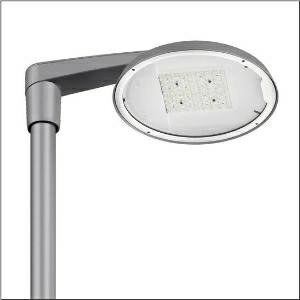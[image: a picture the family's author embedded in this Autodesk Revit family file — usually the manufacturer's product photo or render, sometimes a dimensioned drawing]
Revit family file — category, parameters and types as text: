
# Revit family: dl_50_iq_mini___st0_5a_5xa248b31f08le_1359
name_source: partatom
category: Lighting Fixtures
units: mm (PartAtom-declared; Revit-internal decimal feet)

## family parameters
Cut with Voids When Loaded = No
Host = Face
Light Source = No
Part Type = Normal
Room Calculation Point = No
Round Connector Dimension = Use Diameter
Shared = No

## types (1)
- --- (1 x LED, 10390 lm, 67.4 W, 3000K)
    Apparent Load = 67 VA
    CIE Flux Codes = 41 75 97 100 100
    Color Rendering = 70
    Color Temperature = 3000K
    Default Elevation = 1800 mm
    Description = DL 50 iQ mini, mast luminaire, primary light control with lens, of PMMA, primary optical cover: cover, of toughened safety glass, transparent, light distribution: ST0.5a, light emission: direct distribution, primary light characteristic: asymmetric, installation type: side-entry, post-top, LED, High Power LED, rated luminous flux: 10.390lm, luminous efficacy: 154lm/W, light colour: 730, colour temperature: 3000K, control gear: iQ Street-Remote, control: optimised constant luminous flux control (CLO 2.0), Desk-Remote (wireless, voltage-free reading and setting of iQ features in the workshop via application-optimized NFC function/RFID function), Light-Fading, Smart-Wire, Night-Set, Lumen-Switch, Temp-Guard, Auto-Match, Street-Remote, mains connection: 230..240V, AC, 50/60Hz, connection cable pre-assembled, cable length: 8,5m, start of lifetime: 67W, end of service life: 70W, reduction: 31W, luminaire housing, of diecast aluminium, powder-coated, SITECO metallic grey (DB 702S), inclination adjustable: 0°, 5°, 10° (post-top) | 0°, -5°, -10°, -15° (side-entry), please order mast post-top element or mast side-entry element separately, diameter: 500mm, height: 115mm, post-top: for spigot size d x l = 76 x 100mm; with reducer (optional accessory) 60 x 100mm | side-entry: for spigot size d x l = 60 x 100mm; with reducer (optional accessory) 42 x 100mm, mounting height: 4..6m, protection rating (complete): IP66, insulation class (complete): insulation class II (safety insulation), certification: CE, ENEC, ENEC+, VDE, impact resistance: IK08, permissible operating ambient temperature for outdoor applications: -25..+40°C, standard-compliant lighting for roads and squares, packaging unit: 1 piece

Light Distribution: ST0.5a
    Height = 115 mm
    Lamp = 1 x LED
    Lamp Light Flux = 10390 lm
    Lamp Power = 67.4 W
    Lamp count = 1
    Length = 500 mm
    Luminous efficacy = 154 lm/W
    Manufacturer = Siteco
    ModVariant = No
    Model = 5XA248B31F08LE
    Number of Poles = 1
    OnlyDefault = Yes
    Power Factor = 1
    Product Name = DL 50 iQ mini | ST0.5a
    Product group = mast luminaire | pylon top
    ProductGroupID = 6100
    Protection Class = Protection class II
    Protection Degree = IP 66
    RLX_Detail_Level = 1
    RLX_Emergency_Light_Flux = 0 lm
    RLX_Emergency_Type = 0
    RLX_Emergency_Type_DB = No
    RlxData = <blob elided: 128141 chars, md5=f72b4bb0>
    Socket = socket
    Standby Power = 0 W
    System Light Flux = 10390 lm
    System Power = 67 W
    Type Comments = factory setting: luminous flux: 100 % | dim-lin: 254 | 705 mA
    Type Image = l_1251790.jpg
    URL = http://relux.com
    VarID = @adj_142643
    Voltage = 0 V
    Weight = 0.00 kg
    Width = 0 mm  [stored 0 ft]

note: [stored X ft] marks values corroborated as IEEE doubles in the binary element streams (Revit-internal decimal feet)

## geometry (parser evidence)
native form markers: Blend x4, Sweep x12
no freeform markers — native parametric forms only
